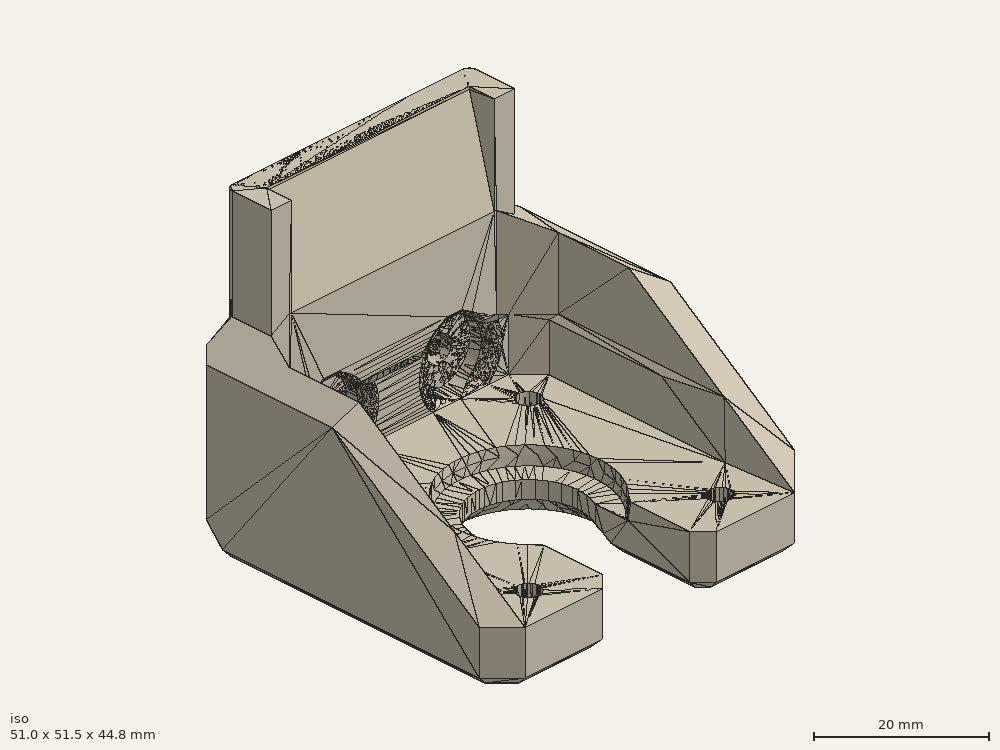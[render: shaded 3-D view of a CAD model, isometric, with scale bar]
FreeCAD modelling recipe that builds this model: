
FCSTD DOCUMENT  (FreeCAD 0.18R14555 (Git shallow))
Label: Z-motor-mount
License: All rights reserved
LicenseURL: http://en.wikipedia.org/wiki/All_rights_reserved
objects: Part::Feature×9, Part::Cut×5, Part::MultiFuse×2, App::Part×1, Part::Box×1, Part::Chamfer×1
note: 18 computed .brp shape members not serialized (recipe doc carries the construction recipe); baked Part::Feature solids carry a one-line shape summary decoded from their .brp

FEATURE [Part::Feature] Part__Feature  label="z_motor_mount"
  Placement = pos=(0,0,8.2) rot=(0,0,1;0rad)
  shape: bbox 51.01 x 51.91 x 44.81 mm, 255 faces (baked)
FEATURE [App::Part] z_motor_mount_v1  label="z_motor_mount v1"
  Group = -> [Part__Feature]
  Origin = -> Origin
FEATURE [Part::Feature] Part__Feature001  label="T-slot-align-chamfer-cut"
  Placement = pos=(4.78,35.3,0) rot=(0,0,-1;1.5708rad)
  shape: bbox 10.45 x 5.4 x 30 mm, 15 faces (baked)
FEATURE [Part::Feature] Part__Feature002  label="T-slot-align-chamfer-cut001"
  Placement = pos=(-15.23,35.3,0) rot=(0,0,-1;1.5708rad)
  shape: bbox 10.45 x 5.4 x 30 mm, 15 faces (baked)
FEATURE [Part::Feature] Part__Feature005  label="m5-to-m4-bolt-hole"
  Placement = pos=(-10,27.5,13.3) rot=(0,0,1;0rad)
  shape: bbox 6 x 3 x 6 mm, 5 faces (baked)
FEATURE [Part::Feature] Part__Feature006  label="m5-to-m4-bolt-hole001"
  Placement = pos=(-10,29.3,13.3) rot=(0,0,1;0rad)
  shape: bbox 6 x 3 x 6 mm, 5 faces (baked)
FEATURE [Part::MultiFuse] Fusion
  Shapes = -> [Part__Feature006,Part__Feature005]
FEATURE [Part::Feature] Fusion001
  Placement = pos=(20,0,0) rot=(0,0,1;0rad)
  shape: bbox 6 x 4.8 x 6 mm, 11 faces (baked)
FEATURE [Part::Box] Box  label="Cube"
  AttacherType = Attacher::AttachEngine3D
  Height = 9
  Length = 60
  Placement = pos=(-28,0,0) rot=(0,0,1;0rad)
  Width = 2
FEATURE [Part::Chamfer] Chamfer
  Base = -> Box
  Edges = 1 edges r=1: [Edge10]
  Placement = pos=(0,29.3,9) rot=(0,0,1;0rad)
FEATURE [Part::Cut] Cut
  Base = -> Part__Feature
  Tool = -> Part__Feature001
FEATURE [Part::Cut] Cut001
  Base = -> Cut
  Tool = -> Part__Feature002
FEATURE [Part::Feature] Part__Feature007  label="t-slot-align"
  Placement = pos=(-4.78,29.3,-1.1e-15) rot=(0,1,0;4.71239rad)
  shape: bbox 10.45 x 5 x 60 mm, 10 faces (baked)
FEATURE [Part::Feature] Part__Feature008  label="t-slot-align001"
  Placement = pos=(15.23,29.3,-3.4e-15) rot=(0,-1,0;1.5708rad)
  shape: bbox 10.45 x 5 x 60 mm, 10 faces (baked)
FEATURE [Part::Cut] Cut002
  Base = -> Cut001
  Tool = -> Part__Feature008
FEATURE [Part::Cut] Cut003
  Base = -> Cut002
  Tool = -> Part__Feature007
FEATURE [Part::Cut] Cut004
  Base = -> Cut003
  Tool = -> Chamfer
FEATURE [Part::MultiFuse] Fusion002
  Shapes = -> [Fusion,Fusion001,Cut004]
FEATURE [Part::Feature] Fusion002001  label="Fusion003"
  shape: bbox 51.01 x 51.51 x 44.81 mm, 238 faces (baked)
